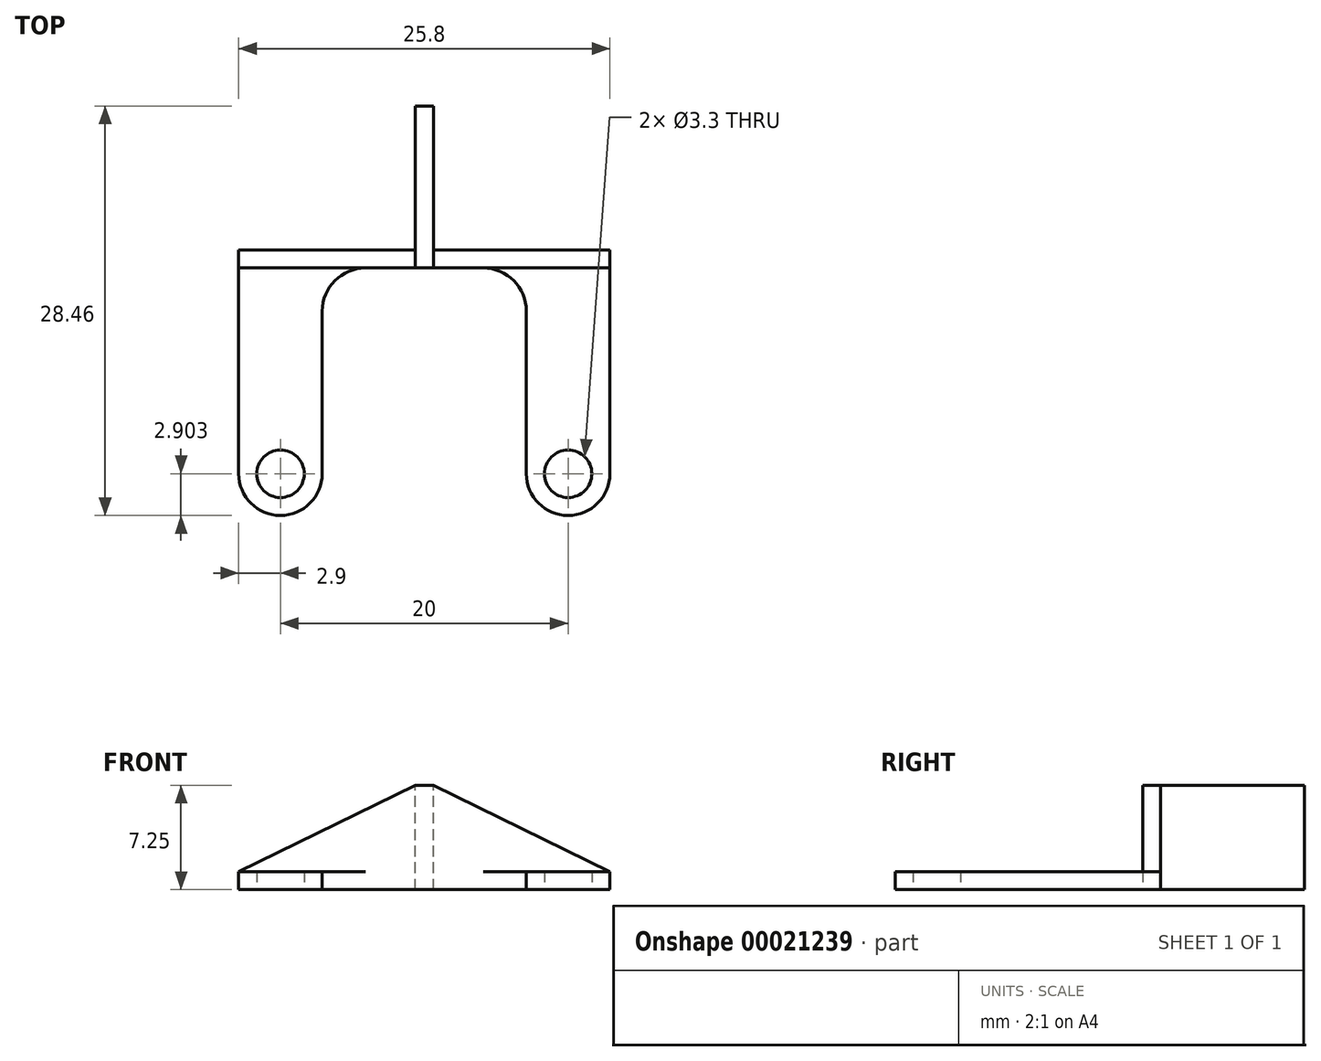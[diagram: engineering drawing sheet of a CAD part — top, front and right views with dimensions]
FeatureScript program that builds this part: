
annotation { "Feature Type Name" : "Feature", "Feature Type Description" : "" }
export const myFeature = defineFeature(function(context is Context, id is Id, definition is map)
    precondition{}
    {
        {
            assignVariable(context, id + "F0", {"name" : "flag_thickness", "anyValue" : (0.44 * 3) * 0.95});
        }
        {
            var Q0;
            Q0=qCreatedBy(makeId("Top.planeOp"),FACE);
            var sketch = newSketch(context, id + "F1", { "sketchPlane" : qUnion([Q0])});
            skLineSegment(sketch, "E0.rect.bottom", {"start": v(12.9, -0.63) * mm, "end": v(-12.9, -0.63) * mm, "construction": true});
            skLineSegment(sketch, "E0.rect.top", {"start": v(12.9, 0.63) * mm, "end": v(-12.9, 0.63) * mm});
            skPoint(sketch, "E0.rect.middle", {"position": v(0, 0) * mm});
            skLineSegment(sketch, "E1", {"start": v(0, 0.63) * mm, "end": v(0, -11.35) * mm, "construction": true});
            skCircle(sketch, "E2", {"center": v(10, -14.93) * mm, "radius": 1.65 * mm});
            skLineSegment(sketch, "E3", {"start": v(12.9, 0.63) * mm, "end": v(12.9, -14.93) * mm});
            skLineSegment(sketch, "E4", {"start": v(7.1, -14.93) * mm, "end": v(7.1, -3.63) * mm});
            skArc(sketch, "E5", {"start": v(7.1, -14.93) * mm, "mid": v(10, -17.83) * mm, "end": v(12.9, -14.93) * mm});
            skArc(sketch, "E6", {"start": v(12.9, -14.93) * mm, "mid": v(10, -12.02) * mm, "end": v(7.1, -14.93) * mm, "construction": true});
            skLineSegment(sketch, "E7.MirrorCS", {"start": v(-12.9, 0.63) * mm, "end": v(-12.9, -14.93) * mm});
            skCircle(sketch, "E8.MirrorC", {"center": v(-10, -14.93) * mm, "radius": 1.65 * mm});
            skArc(sketch, "E9.MirrorCS", {"start": v(-7.1, -14.93) * mm, "mid": v(-10, -17.83) * mm, "end": v(-12.9, -14.93) * mm});
            skLineSegment(sketch, "E10.MirrorCS", {"start": v(-7.1, -14.93) * mm, "end": v(-7.1, -3.63) * mm});
            skLineSegment(sketch, "E11", {"start": v(-4.1, -0.63) * mm, "end": v(4.1, -0.63) * mm});
            skPoint(sketch, "E12.visualSharp", {"position": v(7.1, -0.63) * mm});
            skArc(sketch, "E12.filletArc", {"start": v(7.1, -3.63) * mm, "mid": v(6.22, -1.5) * mm, "end": v(4.1, -0.63) * mm});
            skPoint(sketch, "E13.visualSharp", {"position": v(-7.1, -0.63) * mm});
            skArc(sketch, "E13.filletArc", {"start": v(-4.1, -0.63) * mm, "mid": v(-6.22, -1.5) * mm, "end": v(-7.1, -3.63) * mm});
            skSolve(sketch);
        }
        {
            var Q0;
            Q0 = qSketchRegion(id + "F1", true);
            extrude(context, id + "F2", {"entities" : qUnion([Q0]), "depth" : (getVariable(context, 'flag_thickness')) * mm});
        }
        {
            var Q0;
            Q0=makeQuery(id+"F2.opExtrude","SWEPT_FACE",FACE,{"disambiguationData":[OSD([sQuery(id+"F1.wireOp",EDGE,"E0.rect.top")])]});
            var sketch = newSketch(context, id + "F3", { "sketchPlane" : qUnion([Q0])});
            skLineSegment(sketch, "E14.rect.bottom", {"start": v(0.63, 0) * mm, "end": v(-0.63, 0) * mm});
            skLineSegment(sketch, "E14.rect.top", {"start": v(0.63, 7.25) * mm, "end": v(-0.63, 7.25) * mm});
            skLineSegment(sketch, "E14.rect.left", {"start": v(0.63, 0) * mm, "end": v(0.63, 7.25) * mm});
            skLineSegment(sketch, "E14.rect.right", {"start": v(-0.63, 0) * mm, "end": v(-0.63, 7.25) * mm});
            skPoint(sketch, "E14.rect.middle", {"position": v(0, 3.63) * mm});
            skPoint(sketch, "E14.rect.middle.positionSnap0", {"position": v(0, 1.25) * mm});
            skPoint(sketch, "E14.rect.centerSnap0", {"position": v(0, 1.25) * mm});
            skLineSegment(sketch, "E15", {"start": v(-12.9, 1.25) * mm, "end": v(-0.63, 7.25) * mm});
            skLineSegment(sketch, "E16", {"start": v(0.63, 7.25) * mm, "end": v(12.9, 1.25) * mm});
            skSolve(sketch);
        }
        {
            var Q0;
            {var subQ4=sQuery(id+"F3.wireOp",EDGE,"E15");Q0=makeQuery(id+"F3.imprint","IMPRINT",FACE,{"disambiguationData":[TD([[makeQuery(id+"F3.imprint","IMPRINT",EDGE,{"derivedFrom":subQ4}),-1.0]])]});}
            var Q1;
            {var subQ5=sQuery(id+"F3.wireOp",EDGE,"E14.rect.top");Q1=makeQuery(id+"F3.imprint","IMPRINT",FACE,{"disambiguationData":[TD([[makeQuery(id+"F3.imprint","IMPRINT",EDGE,{"derivedFrom":subQ5}),1.0]])]});}
            var Q2;
            {var subQ4=sQuery(id+"F3.wireOp",EDGE,"E16");Q2=makeQuery(id+"F3.imprint","IMPRINT",FACE,{"disambiguationData":[TD([[makeQuery(id+"F3.imprint","IMPRINT",EDGE,{"derivedFrom":subQ4}),-1.0]])]});}
            var Q3;
            Q3=makeQuery(id+"F2.opExtrude","SWEPT_FACE",FACE,{"disambiguationData":[OSD([sQuery(id+"F1.wireOp",EDGE,"E11")])]});
            extrude(context, id + "F4", {"entities" : qUnion([Q0, Q1, Q2]), "operationType" : NewBodyOperationType.ADD, "endBound" : BoundingType.UP_TO_SURFACE, "oppositeDirection" : true, "endBoundEntityFace" : qUnion([Q3]), "depth" : 25 * mm});
        }
        {
            var Q0;
            {var subQ5=sQuery(id+"F3.wireOp",EDGE,"E14.rect.top");Q0=makeQuery(id+"F3.imprint","IMPRINT",FACE,{"disambiguationData":[TD([[makeQuery(id+"F3.imprint","IMPRINT",EDGE,{"derivedFrom":subQ5}),1.0]])]});}
            var Q1;
            {var subQ7=sQuery(id+"F3.wireOp",EDGE,"E14.rect.bottom");Q1=makeQuery(id+"F3.imprint","IMPRINT",FACE,{"disambiguationData":[TD([[makeQuery(id+"F3.imprint","IMPRINT",EDGE,{"derivedFrom":subQ7}),1.0]])]});}
            extrude(context, id + "F5", {"entities" : qUnion([Q0, Q1]), "operationType" : NewBodyOperationType.ADD, "depth" : 10 * mm});
        }
    });
